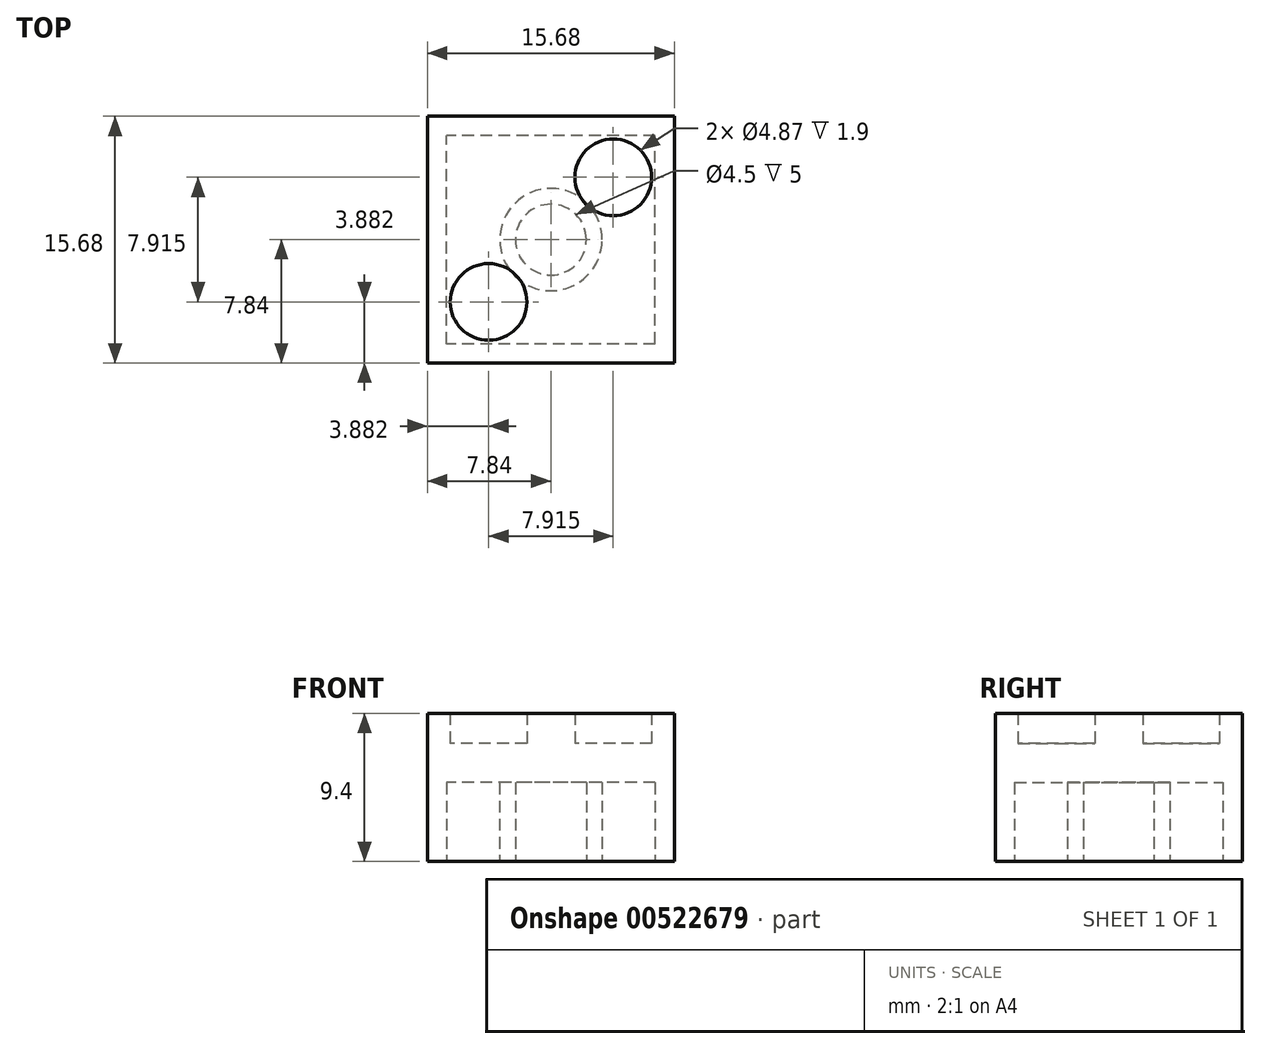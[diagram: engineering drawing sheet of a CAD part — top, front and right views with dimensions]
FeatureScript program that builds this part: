
annotation { "Feature Type Name" : "Feature", "Feature Type Description" : "" }
export const myFeature = defineFeature(function(context is Context, id is Id, definition is map)
    precondition{}
    {
        {
            assignVariable(context, id + "F0", {"name" : "Height", "anyValue" : 10});
        }
        {
            assignVariable(context, id + "F1", {"name" : "PegHeight", "anyValue" : 1.9});
        }
        {
            var Q0;
            Q0=qCreatedBy(makeId("Top.planeOp"),FACE);
            var sketch = newSketch(context, id + "F2", { "sketchPlane" : qUnion([Q0])});
            skLineSegment(sketch, "E0.bottom", {"start": v(7.84, -7.84) * mm, "end": v(-7.84, -7.84) * mm});
            skLineSegment(sketch, "E0.top", {"start": v(7.84, 7.84) * mm, "end": v(-7.84, 7.84) * mm});
            skLineSegment(sketch, "E0.left", {"start": v(7.84, -7.84) * mm, "end": v(7.84, 7.84) * mm});
            skLineSegment(sketch, "E0.right", {"start": v(-7.84, -7.84) * mm, "end": v(-7.84, 7.84) * mm});
            skPoint(sketch, "E0.middle", {"position": v(0, 0) * mm});
            skLineSegment(sketch, "E1.0", {"start": v(6.62, 6.62) * mm, "end": v(-6.62, 6.62) * mm});
            skLineSegment(sketch, "E1.1", {"start": v(6.62, -6.62) * mm, "end": v(6.62, 6.62) * mm});
            skLineSegment(sketch, "E1.2", {"start": v(6.62, -6.62) * mm, "end": v(-6.62, -6.62) * mm});
            skLineSegment(sketch, "E1.3", {"start": v(-6.62, -6.62) * mm, "end": v(-6.62, 6.62) * mm});
            skCircle(sketch, "E2", {"center": v(0, 0) * mm, "radius": 3.25 * mm});
            skCircle(sketch, "E3.0", {"center": v(0, 0) * mm, "radius": 2.25 * mm});
            skSolve(sketch);
        }
        {
            var Q0;
            Q0=makeQuery(id+"F2.imprint","IMPRINT",FACE,{"disambiguationData":[TD([[makeQuery(id+"F2.imprint","IMPRINT",EDGE,{"derivedFrom":sQuery(id+"F2.wireOp",EDGE,"E0.bottom")}),-1.0]])]});
            var Q1;
            Q1=makeQuery(id+"F2.imprint","IMPRINT",FACE,{"disambiguationData":[TD([[makeQuery(id+"F2.imprint","IMPRINT",EDGE,{"derivedFrom":sQuery(id+"F2.wireOp",EDGE,"E2")}),1.0]])]});
            extrude(context, id + "F3", {"entities" : qUnion([Q0, Q1]), "depth" : (getVariable(context, 'Height') / 2) * mm, "offsetDistance" : 25 * mm});
        }
        {
            var Q0;
            Q0=qCreatedBy(makeId("Top.planeOp"),FACE);
            cPlane(context, id + "F4", {"entities" : qUnion([Q0]), "cplaneType" : CPlaneType.OFFSET, "offset" : (getVariable(context, 'Height') / 2) * mm, "width" : 150 * mm, "height" : 150 * mm});
        }
        {
            var Q0;
            Q0=qCreatedBy(id+"F4.planeOp",FACE);
            var sketch = newSketch(context, id + "F5", { "sketchPlane" : qUnion([Q0])});
            skLineSegment(sketch, "E4.bottom", {"start": v(7.84, -7.84) * mm, "end": v(-7.84, -7.84) * mm});
            skLineSegment(sketch, "E4.top", {"start": v(7.84, 7.84) * mm, "end": v(-7.84, 7.84) * mm});
            skLineSegment(sketch, "E4.left", {"start": v(7.84, -7.84) * mm, "end": v(7.84, 7.84) * mm});
            skLineSegment(sketch, "E4.right", {"start": v(-7.84, -7.84) * mm, "end": v(-7.84, 7.84) * mm});
            skPoint(sketch, "E4.middle", {"position": v(0, 0) * mm});
            skSolve(sketch);
        }
        {
            var Q0;
            Q0=makeQuery(id+"F5.imprint","IMPRINT",FACE,{"disambiguationData":[TD([[makeQuery(id+"F5.imprint","IMPRINT",EDGE,{"derivedFrom":sQuery(id+"F5.wireOp",EDGE,"E4.bottom")}),-1.0]])]});
            extrude(context, id + "F6", {"entities" : qUnion([Q0]), "operationType" : NewBodyOperationType.ADD, "depth" : 2.5 * mm, "offsetDistance" : 25 * mm});
        }
        {
            var Q0;
            Q0=makeQuery(id+"F6.opExtrude","CAP_FACE",FACE,{"disambiguationData":[OSD([sQuery(id+"F5.wireOp",EDGE,"E4.bottom"),sQuery(id+"F5.wireOp",EDGE,"E4.top"),sQuery(id+"F5.wireOp",EDGE,"E4.left"),sQuery(id+"F5.wireOp",EDGE,"E4.right")])],"isStart":false});
            var sketch = newSketch(context, id + "F7", { "sketchPlane" : qUnion([Q0])});
            skPoint(sketch, "E5.startSnap0", {"position": v(-7.84, 0) * mm});
            skPoint(sketch, "E6.orphan", {"position": v(0, 7.84) * mm});
            skPoint(sketch, "E7.orphan", {"position": v(7.84, 0) * mm});
            skLineSegment(sketch, "E8", {"start": v(0, 7.84) * mm, "end": v(0, -7.84) * mm, "construction": true});
            skLineSegment(sketch, "E9", {"start": v(0, 0) * mm, "end": v(3.96, 0) * mm, "construction": true});
            skPoint(sketch, "E9.endSnap0", {"position": v(0, 0) * mm});
            skLineSegment(sketch, "E10", {"start": v(3.96, 0) * mm, "end": v(3.96, -3.96) * mm, "construction": true});
            skCircle(sketch, "E11", {"center": v(3.96, -3.96) * mm, "radius": 2.44 * mm});
            skCircle(sketch, "E12.MirrorC", {"center": v(3.96, 3.96) * mm, "radius": 2.44 * mm});
            skCircle(sketch, "E13.MirrorC", {"center": v(-3.96, -3.96) * mm, "radius": 2.44 * mm});
            skCircle(sketch, "E14.MirrorC", {"center": v(-3.96, 3.96) * mm, "radius": 2.44 * mm});
            skSolve(sketch);
        }
        {
            var Q0;
            Q0=makeQuery(id+"F7.imprint","IMPRINT",FACE,{"disambiguationData":[TD([[makeQuery(id+"F7.imprint","IMPRINT",EDGE,{"derivedFrom":sQuery(id+"F7.wireOp",EDGE,"E14.MirrorC")}),1.0]])]});
            var Q1;
            Q1=makeQuery(id+"F7.imprint","IMPRINT",FACE,{"disambiguationData":[TD([[makeQuery(id+"F7.imprint","IMPRINT",EDGE,{"derivedFrom":sQuery(id+"F7.wireOp",EDGE,"E13.MirrorC")}),-1.0]])]});
            var Q2;
            Q2=makeQuery(id+"F7.imprint","IMPRINT",FACE,{"disambiguationData":[TD([[makeQuery(id+"F7.imprint","IMPRINT",EDGE,{"derivedFrom":sQuery(id+"F7.wireOp",EDGE,"E11")}),1.0]])]});
            var Q3;
            Q3=makeQuery(id+"F7.imprint","IMPRINT",FACE,{"disambiguationData":[TD([[makeQuery(id+"F7.imprint","IMPRINT",EDGE,{"derivedFrom":sQuery(id+"F7.wireOp",EDGE,"E12.MirrorC")}),-1.0]])]});
            extrude(context, id + "F8", {"entities" : qUnion([Q0, Q1, Q2, Q3]), "operationType" : NewBodyOperationType.ADD, "depth" : (getVariable(context, 'PegHeight')) * mm, "offsetDistance" : 25 * mm});
        }
    });
